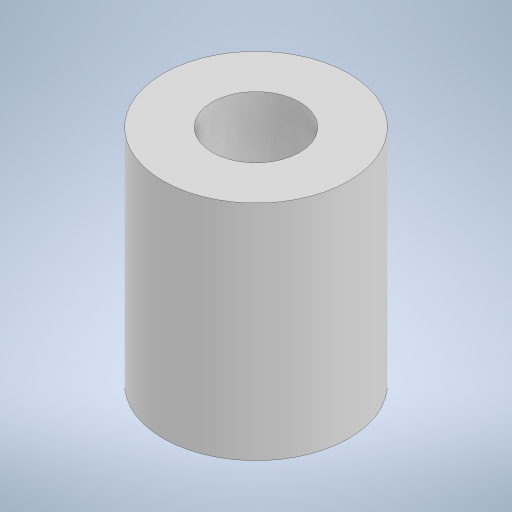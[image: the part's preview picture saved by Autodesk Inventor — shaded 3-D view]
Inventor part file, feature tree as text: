
AUTODESK INVENTOR PART (.ipt)
format: ipt  version: 2024.2 (Build 282272000, 272)  size: 196,608 bytes
history: native  units: mm
features: extrude x1, sketch x1
ambient origin geometry x8: Origin, YZ Plane, XZ Plane, XY Plane, X Axis, Y Axis, Z Axis, Center Point
bodies: Solid1 (feature_tree)
feature tree (2):
  extrude  "Extrusion1"  Depth=10.0mm
  sketch  "Sketch1"  dims[d0=4.7mm d1=10.0mm d2=12.0mm d3=0.0mm]
